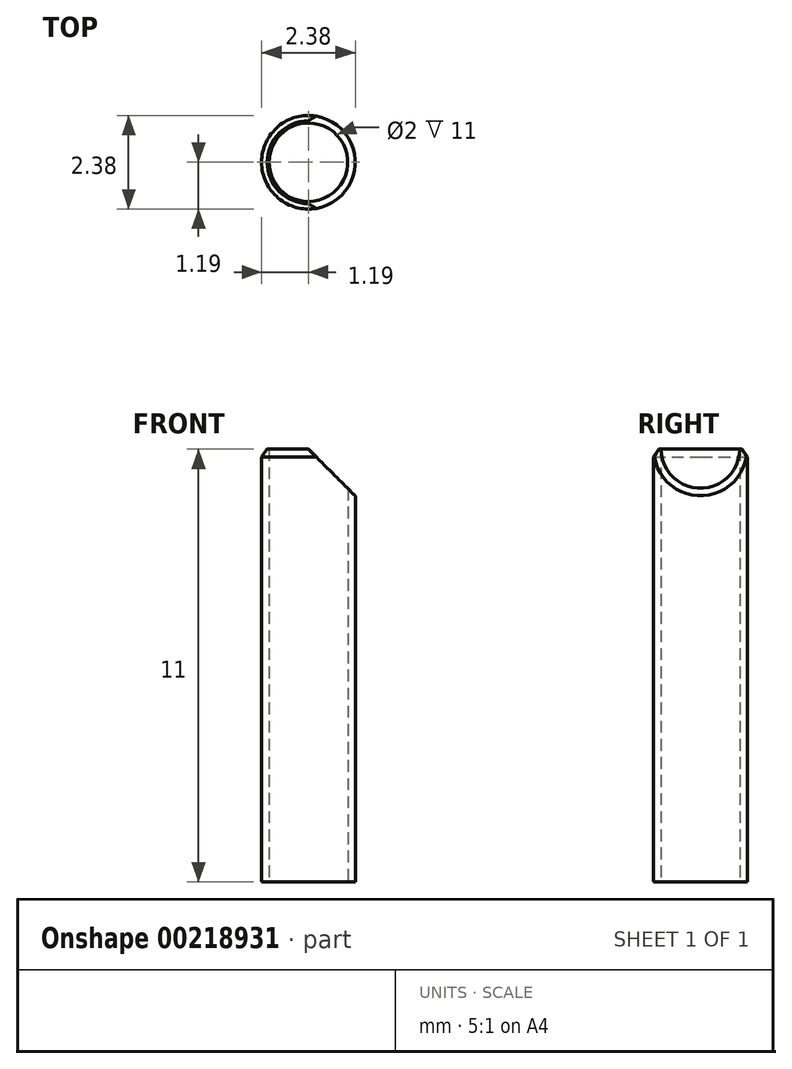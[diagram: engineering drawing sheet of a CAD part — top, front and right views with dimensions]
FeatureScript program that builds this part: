
annotation { "Feature Type Name" : "Feature", "Feature Type Description" : "" }
export const myFeature = defineFeature(function(context is Context, id is Id, definition is map)
    precondition{}
    {
        {
            var Q0;
            Q0=qCreatedBy(makeId("Right.planeOp"),FACE);
            var sketch = newSketch(context, id + "F0", { "sketchPlane" : qUnion([Q0])});
            skLineSegment(sketch, "E0", {"start": v(0, 0) * mm, "end": v(0, 11) * mm});
            skLineSegment(sketch, "E1", {"start": v(0, 11) * mm, "end": v(-1.05, 11) * mm});
            skLineSegment(sketch, "E2", {"start": v(-1.2, 10.8) * mm, "end": v(-1.19, 0) * mm});
            skLineSegment(sketch, "E3", {"start": v(-1.19, 0) * mm, "end": v(0, 0) * mm});
            skLineSegment(sketch, "E4", {"start": v(-1.05, 11) * mm, "end": v(-1.2, 10.8) * mm});
            skSolve(sketch);
        }
        {
            var Q0;
            Q0=makeQuery(id+"F0.imprint","IMPRINT",FACE,{"disambiguationData":[TD([[makeQuery(id+"F0.imprint","IMPRINT",EDGE,{"derivedFrom":sQuery(id+"F0.wireOp",EDGE,"E0")}),1.0]])]});
            var Q1;
            Q1=sQuery(id+"F0.wireOp",EDGE,"E0");
            revolve(context, id + "F1", {"entities" : qUnion([Q0]), "axis" : qUnion([Q1]), "revolveType" : RevolveType.FULL});
        }
        {
            var Q0;
            Q0=qCreatedBy(makeId("Top.planeOp"),FACE);
            var sketch = newSketch(context, id + "F2", { "sketchPlane" : qUnion([Q0])});
            skCircle(sketch, "E5", {"center": v(0, 0) * mm, "radius": 1 * mm});
            skSolve(sketch);
        }
        {
            var Q0;
            Q0=qSketchRegion(id+"F2",true);
            extrude(context, id + "F3", {"entities" : qUnion([Q0]), "operationType" : NewBodyOperationType.REMOVE, "depth" : 100 * mm});
        }
        {
            var Q0;
            Q0=qCreatedBy(makeId("Front.planeOp"),FACE);
            var sketch = newSketch(context, id + "F4", { "sketchPlane" : qUnion([Q0])});
            skLineSegment(sketch, "E6", {"start": v(0, 11) * mm, "end": v(2.24, 11) * mm});
            skLineSegment(sketch, "E7", {"start": v(2.24, 11) * mm, "end": v(2.24, 8.76) * mm});
            skLineSegment(sketch, "E8", {"start": v(2.24, 8.76) * mm, "end": v(0, 11) * mm});
            skSolve(sketch);
        }
        {
            var Q0;
            Q0=qSketchRegion(id+"F4",true);
            extrude(context, id + "F5", {"entities" : qUnion([Q0]), "operationType" : NewBodyOperationType.REMOVE, "oppositeDirection" : true, "depth" : 5 * mm});
        }
        {
            var Q0;
            Q0=qSketchRegion(id+"F4",true);
            extrude(context, id + "F6", {"entities" : qUnion([Q0]), "operationType" : NewBodyOperationType.REMOVE, "depth" : 25 * mm});
        }
    });
